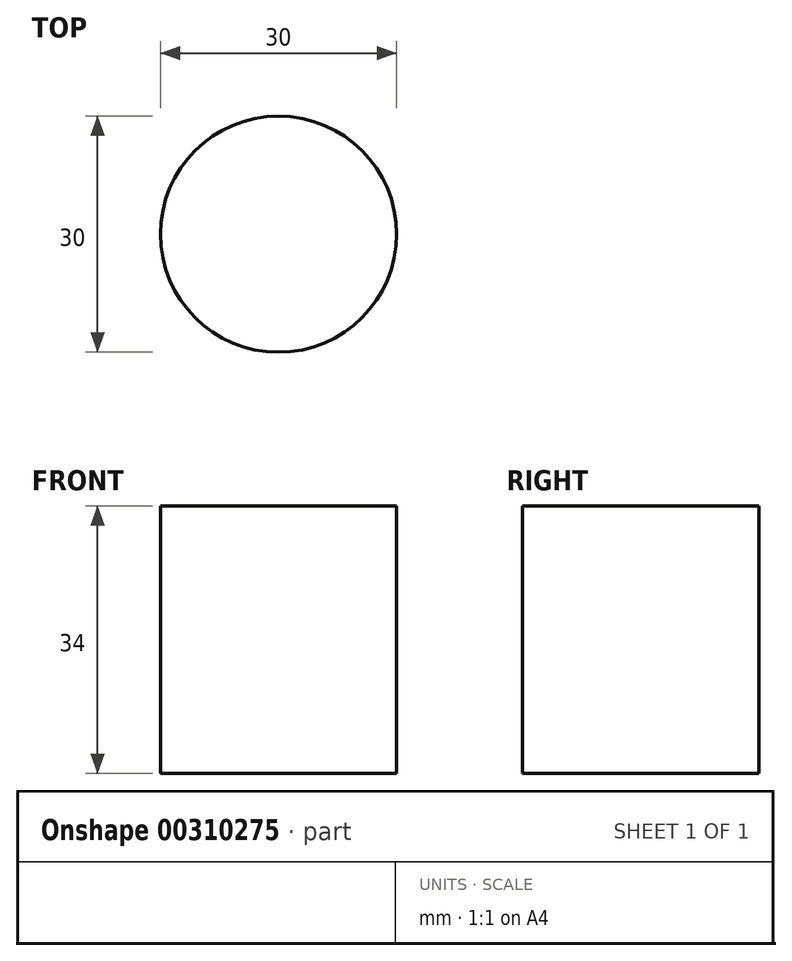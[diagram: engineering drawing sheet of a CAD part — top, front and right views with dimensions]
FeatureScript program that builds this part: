
annotation { "Feature Type Name" : "Feature", "Feature Type Description" : "" }
export const myFeature = defineFeature(function(context is Context, id is Id, definition is map)
    precondition{}
    {
        {
            var Q0;
            Q0=qCreatedBy(makeId("Top.planeOp"),FACE);
            var sketch = newSketch(context, id + "F0", { "sketchPlane" : qUnion([Q0])});
            skCircle(sketch, "E0", {"center": v(0, 0) * mm, "radius": 15 * mm});
            skSolve(sketch);
        }
        {
            var Q0;
            Q0=makeQuery(id+"F0.imprint","IMPRINT",FACE,{"disambiguationData":[TD([[makeQuery(id+"F0.imprint","IMPRINT",EDGE,{"derivedFrom":sQuery(id+"F0.wireOp",EDGE,"E0")}),1.0]])]});
            extrude(context, id + "F1", {"entities" : qUnion([Q0]), "depth" : 34 * mm});
        }
    });
